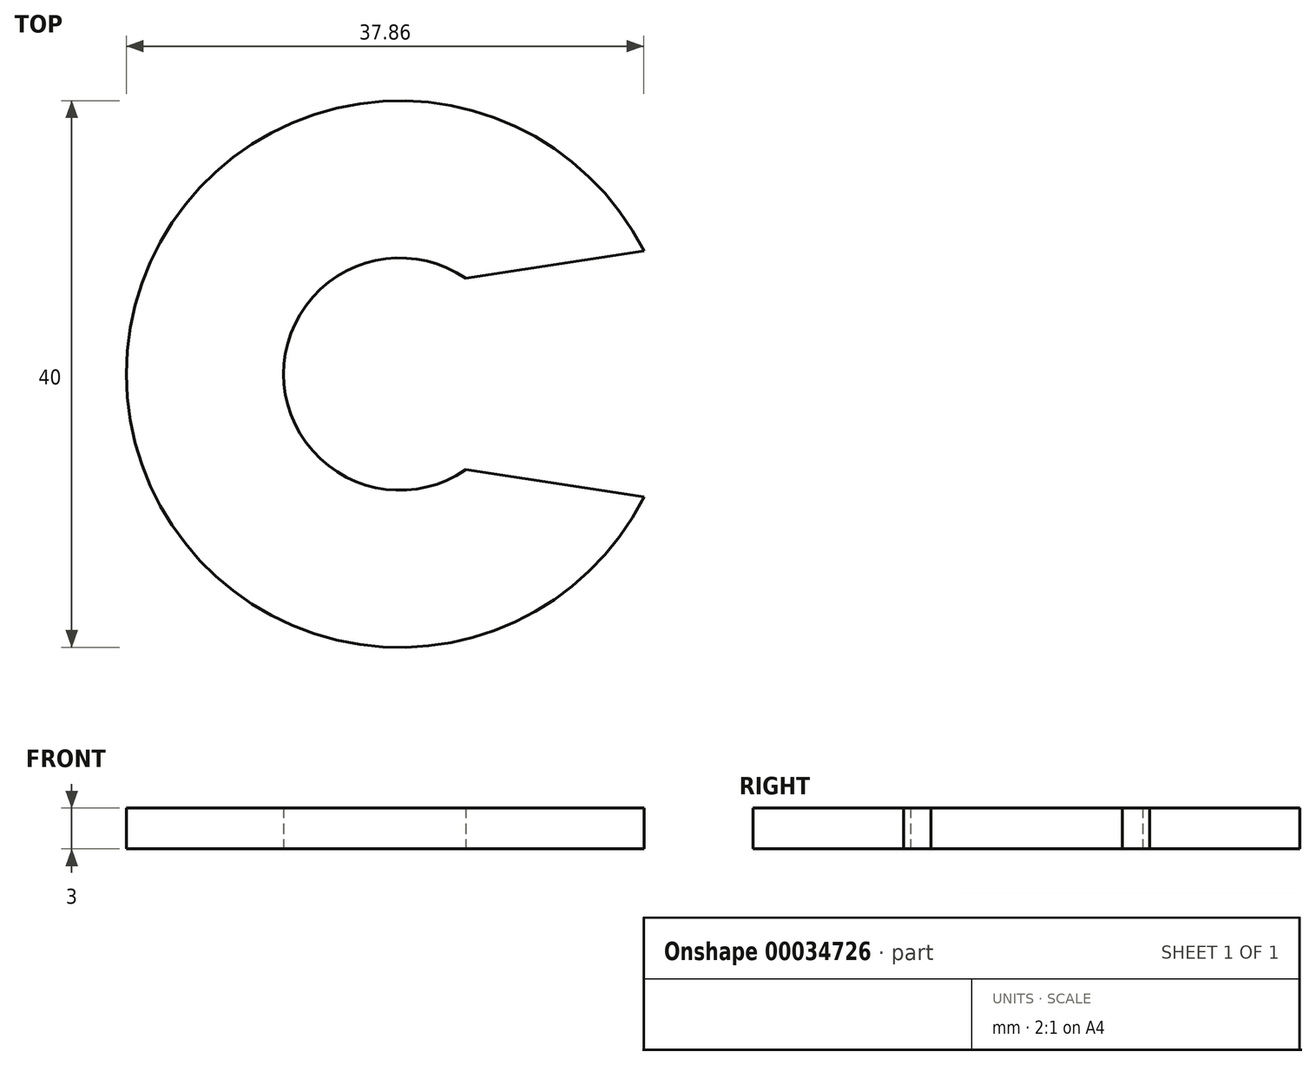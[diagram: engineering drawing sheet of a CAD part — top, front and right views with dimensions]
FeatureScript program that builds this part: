
annotation { "Feature Type Name" : "Feature", "Feature Type Description" : "" }
export const myFeature = defineFeature(function(context is Context, id is Id, definition is map)
    precondition{}
    {
        {
            var Q0;
            Q0=qCreatedBy(makeId("Top.planeOp"),FACE);
            var sketch = newSketch(context, id + "F0", { "sketchPlane" : qUnion([Q0])});
            skCircle(sketch, "E0", {"center": v(0, 0) * mm, "radius": 20 * mm});
            skCircle(sketch, "E1", {"center": v(0, 0) * mm, "radius": 8.5 * mm});
            skLineSegment(sketch, "E2", {"start": v(4.82, 7) * mm, "end": v(17.86, 9) * mm});
            skLineSegment(sketch, "E3", {"start": v(0, 0) * mm, "end": v(20, 0) * mm, "construction": true});
            skLineSegment(sketch, "E4.MirrorCS", {"start": v(4.82, -7) * mm, "end": v(17.86, -9) * mm});
            skLineSegment(sketch, "E5", {"start": v(17.86, -9) * mm, "end": v(17.86, 9) * mm, "construction": true});
            skLineSegment(sketch, "E6", {"start": v(4.82, -7) * mm, "end": v(4.82, 7) * mm, "construction": true});
            skSolve(sketch);
        }
        {
            var Q0;
            {var subQ0=sQuery(id+"F0.wireOp",EDGE,"E2");Q0=makeQuery(id+"F0.imprint","IMPRINT",FACE,{"disambiguationData":[TD([[makeQuery(id+"F0.imprint","IMPRINT",EDGE,{"derivedFrom":subQ0}),1.0]])]});}
            extrude(context, id + "F1", {"entities" : qUnion([Q0]), "depth" : 3 * mm});
        }
    });
